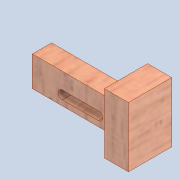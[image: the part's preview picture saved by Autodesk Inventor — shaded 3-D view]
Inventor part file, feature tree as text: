
AUTODESK INVENTOR PART (.ipt)
format: ipt  version: 2020 (Build 240168000, 168)  size: 279,552 bytes
history: native  units: mm
features: extrude x4, sketch x4, fillet x1
ambient origin geometry x8: Origin, YZ Plane, XZ Plane, XY Plane, X Axis, Y Axis, Z Axis, Center Point
bodies: Solid1 (feature_tree)
feature tree (9):
  extrude  "Extrusion1"  Depth=25.0mm
  extrude  "Extrusion5"  Depth=3.5mm
  extrude  "Extrusion6"  Depth=4.0mm
  extrude  "Extrusion7"  Depth=2.0mm
  fillet  "Fillet2"  Radius=15.0mm
  sketch  "Sketch1"  dims[d0=50.0mm d1=25.0mm]
  sketch  "Sketch5"  dims[d2=18.0mm d3=0.0mm d29=3.5mm]
  sketch  "Sketch6"  dims[d30=4.0mm d31=4.0mm]
  sketch  "Sketch7"  dims[d32=20.0mm d33=15.0mm d34=15.0mm d35=0.0mm d36=10.0mm d37=10.0mm d38=0.0mm d40=10.0mm d41=0.0mm d42=2.0mm]
